# Revit family: EP3003-1.9
name_source: partatom
category: Aparatos sanitarios
units: mm (PartAtom-declared; Revit-internal decimal feet)

## family parameters
Compartido = No
Corte con vacíos al cargar = No
Cota de conector redondo = Diámetro de uso
Número OmniClass = 23.45.00.00
Punto de cálculo de habitación = No
Se basa en plano de trabajo = No
Siempre vertical = Sí
Tipo de pieza = Normal
Título OmniClass = Sanitary, Laundry, and Cleaning Equipment

## types (1)
- EP3003-1.9
    Accesorios = Placa para empotrar en tablaroca, Llave para aireador, Llave allen 5/64", Llave de instalación
    Chrome = Brass Chromed
    Comentarios de tipo = Ensambles Básicos para Lavabo
    Conexión AC = Sí
    Conexión AF = Sí
    Descripción = Monomando de lavabo a pared con contra tipo
    Elevación por defecto = 45"
    Fabricante = Helvex
    Features = Monomando de lavabo a pared con contra tipo
hongo sin rebosadero.
    Inlet Threads = ½" - 14 NPSM
    Max. Working Pressure = 85.3 psi
    Min. Working Pressure = 5.5 psi
    Modelo = EP3003-1.9
    Operación = El maneral tiene una rotación horizontal para la función de agua caliente y fría; y vertical para abrir y cerrar el flujo de agua.
    Support Base Diameter = 2"
    Total Length = 9"
    Total Width = 4"

## geometry (parser evidence)
native form markers: Sweep x3
no freeform markers — native parametric forms only
